# Revit family: Camera-Security-Panasonic-Super_Dynamic-Vandal_Resistant-Dome-Network-S2231LSeriesX
name_source: partatom
category: Security Devices
revit_build: Autodesk Revit 2013 (Build: 20130531_2115(x64)
units: mm (PartAtom-declared; Revit-internal decimal feet)

## types (2) — shared parameters
Alarm Input Or Output Specification = ALARM IN 1 (DAY/NIGHT IN, Auto time adjustment) (x1),ALARM IN 2 (ALARM OUT) (x1), ALARM IN 3 (AUX OUT) (x1)
Angle Of View = 110
Audio In = Yes
Audio Out = Yes
Communication Ports = 10Base-T / 100Base-TX, RJ45 connector
Date Last Modified = 2016/10/31
Day Or Night = Yes
Diameter = 5.098 "
Dome Part Number = WV-CR1S
Equipment Abbreviation = SC
Family Version = 1.0.0
HFOV Max 169 = 110.00°
HFOV Max 43 = 90.00°
HFOV Min 169 = 30.00°
HFOV Min 43 = 25.00°
Has POE = Yes
Height = 4.035 "
IP Or Analog = IP
Indoor Or Outdoor = Indoor
Manufacturer = Panasonic
Model Disclaimer = Contact Panasonic for more information
Mounting Positions = Surface Mount
Operational Humidity = 10% to 90% (no condensation)
Operational Temperature = 14°F - 122°F
PPM Target Height = 7.008 "
Pan Max = 120.00°
Pan Min = -240.00°
Panning Range = -240 to +120
Power Active = 6.8 W
Product Documentation Link = http://ssbu-t.psn-web.net
Product Material = Paint - Panasonic - Sail White
Product Page URL = http://security.panasonic.com
Provide Feedback = https://www.surveymonkey.com
Regulatory Compliance = UL UL60950-1, C-UL CAN/CSA C22.2 No.60950-1, CE, IEC60950-1 FCC Part15 ClassA, ICES003 ClassA, EN55022 ClassB, EN55024
Shock Resistance = Compliant with IK10 (IEC 62262)
Storage Temperature = 14°F - 122°F
Tilt Max = 85.00°
Tilt Min = -30.00°
Tilting Range = -30 to +85
URL = http://security.panasonic.com
VFOV Max 169 = 59.00°
VFOV Max 43 = 66.00°
VFOV Min 169 = 17.00°
VFOV Min 43 = 19.00°
Vandal Resistant = Yes
Voltage DC = 12 V
Weight = 1.65 lb
Wide Dynamic Range = Yes
Yaw Max = 100.00°
Yaw Min = -100.00°
Yawing Range = -100 to +100
z Base Height = 2.205 "
z Base Radius = 2.549 "
z Bracket Radius = 3.661 "
z Const Pan Handle Length = 19.488 "
z Const Tilt Base Length = 9.843 "
z Const Tilt Base2 Length = 19.685 "
z Const Tilt Handle Length = 11.811 "
z Const Yaw Base Length = 10.236 "
z Const Yaw Base2 Length = 17.323 "
z Const Yaw Handle Length = 9.252 "
z Dome Material = Glass - Panasonic - Smoked
z Dome Radius = 1.831 "
z Type = 1
z VV Viewpoint Depth Max = 1.22 "
z VV Viewpoint Depth Min = 0.866 "
zero-valued in all types: Default Elevation, z VV Origin Horizontal Offset, z Zero

## per-type parameters (varying)
| type | Description | Minimum Illumination | Part Description | z Camera Resolution Type |
| WV-S2231L | Security Camera, Fixed Dome, Network, Super Dynamic Vandal Resistant FullHD | 0.012 lx | Security Camera, Fixed Dome, Network, Super Dynamic Vandal Resistant FullHD | 1 |
| WV-S2211L | Security Camera, Fixed Dome, Network, Super Dynamic HD | 0.008 lx | Security Camera, Fixed Dome, Network, Super Dynamic HD | 2 |

note: column(s) folded — value = type name in every type: Model, Part Number

## geometry (parser evidence)
native form markers: Sweep x6
no freeform markers — native parametric forms only
